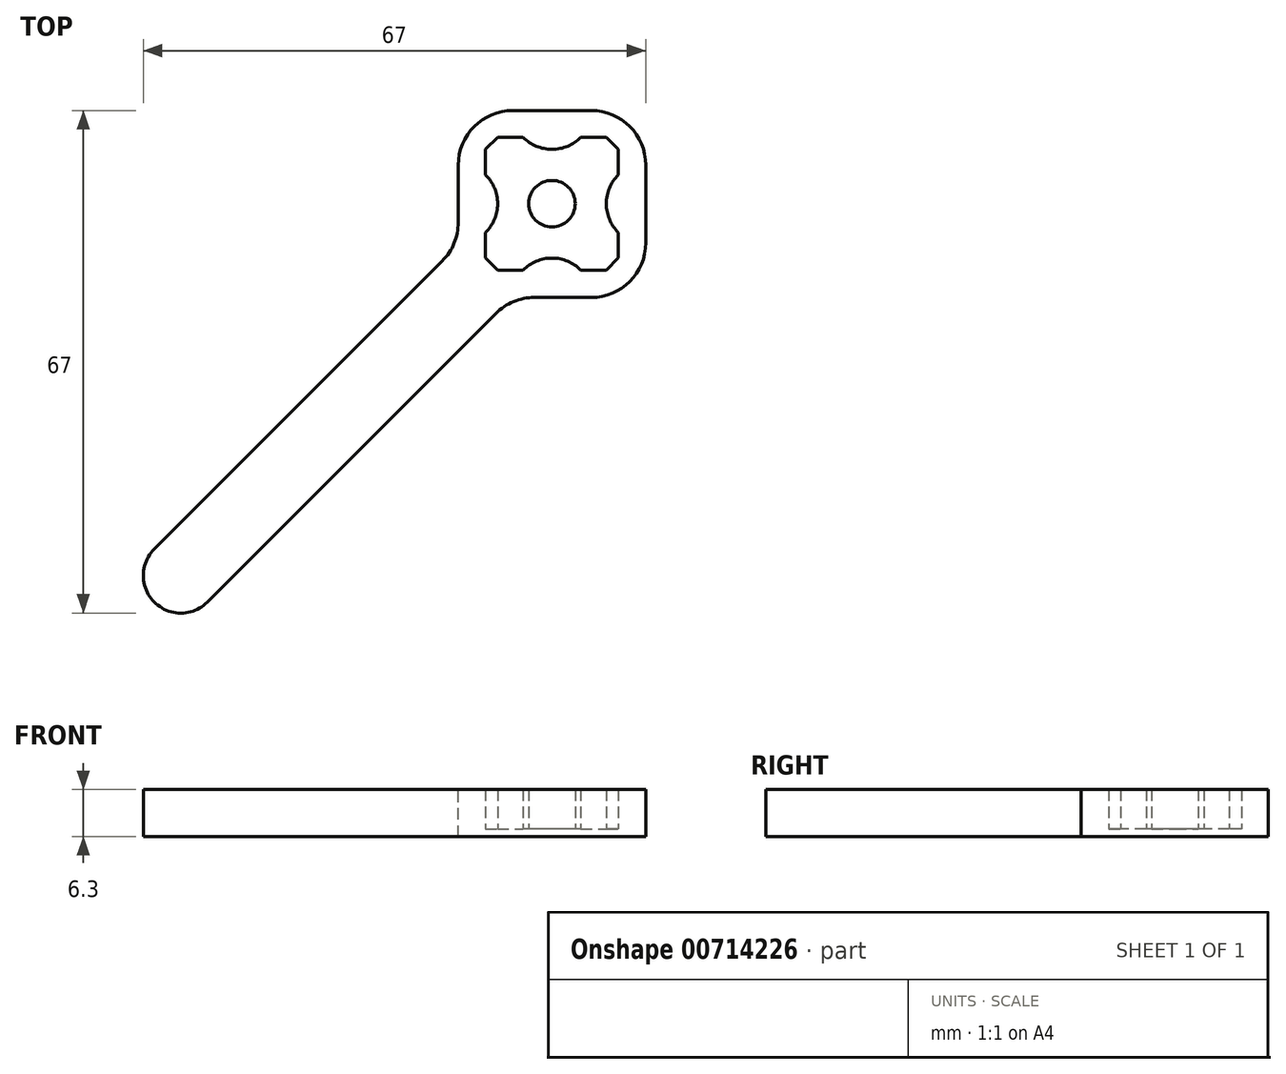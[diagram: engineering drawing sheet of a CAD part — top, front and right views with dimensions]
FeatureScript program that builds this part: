
annotation { "Feature Type Name" : "Feature", "Feature Type Description" : "" }
export const myFeature = defineFeature(function(context is Context, id is Id, definition is map)
    precondition{}
    {
        {
            var Q0;
            Q0=qCreatedBy(makeId("Top.planeOp"),FACE);
            var sketch = newSketch(context, id + "F0", { "sketchPlane" : qUnion([Q0])});
            skPoint(sketch, "E0", {"position": v(-49.5, -49.5) * mm});
            skArc(sketch, "E1", {"start": v(-53.03, -45.96) * mm, "mid": v(-53.03, -53.03) * mm, "end": v(-45.96, -53.03) * mm});
            skLineSegment(sketch, "E2", {"start": v(-5.35, -12.42) * mm, "end": v(-45.96, -53.03) * mm});
            skLineSegment(sketch, "E3", {"start": v(-53.03, -45.96) * mm, "end": v(-12.5, -5.43) * mm});
            skLineSegment(sketch, "E4.bottom", {"start": v(12.5, -12.5) * mm, "end": v(-5.43, -12.5) * mm});
            skLineSegment(sketch, "E4.top", {"start": v(12.5, 12.5) * mm, "end": v(-12.5, 12.5) * mm});
            skLineSegment(sketch, "E4.left", {"start": v(12.5, -12.5) * mm, "end": v(12.5, 12.5) * mm});
            skPoint(sketch, "E4.middle", {"position": v(0, 0) * mm});
            skLineSegment(sketch, "E5.bottom", {"start": v(12.5, 12.58) * mm, "end": v(-12.5, 12.58) * mm});
            skLineSegment(sketch, "E5.top", {"start": v(12.5, -12.42) * mm, "end": v(-5.35, -12.42) * mm});
            skLineSegment(sketch, "E5.left", {"start": v(12.5, 12.58) * mm, "end": v(12.5, -12.42) * mm});
            skLineSegment(sketch, "E5.right", {"start": v(-12.5, 12.58) * mm, "end": v(-12.5, -5.43) * mm});
            skPoint(sketch, "E5.middle", {"position": v(0, 0.08) * mm});
            skLineSegment(sketch, "E6.bottom", {"start": v(-7.25, 8.93) * mm, "end": v(-3.85, 8.93) * mm});
            skLineSegment(sketch, "E6.top", {"start": v(-7.25, -8.77) * mm, "end": v(-3.85, -8.77) * mm});
            skLineSegment(sketch, "E6.left", {"start": v(-8.85, 7.33) * mm, "end": v(-8.85, 3.93) * mm});
            skLineSegment(sketch, "E6.right", {"start": v(8.85, 7.33) * mm, "end": v(8.85, 3.93) * mm});
            skPoint(sketch, "E7", {"position": v(-3.85, 8.93) * mm});
            skPoint(sketch, "E8", {"position": v(3.85, 8.93) * mm});
            skPoint(sketch, "E9", {"position": v(8.85, 3.93) * mm});
            skPoint(sketch, "E10", {"position": v(8.85, -3.77) * mm});
            skPoint(sketch, "E11", {"position": v(3.85, -8.77) * mm});
            skPoint(sketch, "E12", {"position": v(-3.85, -8.77) * mm});
            skPoint(sketch, "E13", {"position": v(-8.85, -3.77) * mm});
            skPoint(sketch, "E14", {"position": v(-8.85, 3.93) * mm});
            skPoint(sketch, "E15", {"position": v(-7.25, 0.08) * mm});
            skPoint(sketch, "E16", {"position": v(0, 7.33) * mm});
            skPoint(sketch, "E17", {"position": v(7.25, 0.08) * mm});
            skPoint(sketch, "E18", {"position": v(0, -7.17) * mm});
            skArc(sketch, "E19", {"start": v(-3.85, 8.93) * mm, "mid": v(0, 7.33) * mm, "end": v(3.85, 8.93) * mm});
            skArc(sketch, "E20", {"start": v(8.85, 3.93) * mm, "mid": v(7.25, 0.08) * mm, "end": v(8.85, -3.77) * mm});
            skArc(sketch, "E21", {"start": v(3.85, -8.77) * mm, "mid": v(0, -7.17) * mm, "end": v(-3.85, -8.77) * mm});
            skArc(sketch, "E22", {"start": v(-8.85, -3.77) * mm, "mid": v(-7.25, 0.08) * mm, "end": v(-8.85, 3.93) * mm});
            skPoint(sketch, "E23.orphan", {"position": v(7.25, 7.33) * mm});
            skPoint(sketch, "E24.orphan", {"position": v(-7.25, 7.33) * mm});
            skPoint(sketch, "E25.orphan", {"position": v(-7.25, -7.17) * mm});
            skPoint(sketch, "E26.left.end.orphan", {"position": v(7.25, -7.17) * mm});
            skLineSegment(sketch, "E27.trimOffspring", {"start": v(3.85, 8.93) * mm, "end": v(7.25, 8.93) * mm});
            skLineSegment(sketch, "E28.trimOffspring", {"start": v(8.85, -3.77) * mm, "end": v(8.85, -7.17) * mm});
            skLineSegment(sketch, "E29.trimOffspring", {"start": v(3.85, -8.77) * mm, "end": v(7.25, -8.77) * mm});
            skLineSegment(sketch, "E30.trimOffspring", {"start": v(-8.85, -3.77) * mm, "end": v(-8.85, -7.17) * mm});
            skPoint(sketch, "E31", {"position": v(7.25, 8.93) * mm});
            skPoint(sketch, "E32", {"position": v(8.85, 7.33) * mm});
            skPoint(sketch, "E33", {"position": v(8.85, -7.17) * mm});
            skPoint(sketch, "E34", {"position": v(7.25, -8.77) * mm});
            skPoint(sketch, "E35", {"position": v(-7.25, -8.77) * mm});
            skPoint(sketch, "E36", {"position": v(-8.85, -7.17) * mm});
            skPoint(sketch, "E37", {"position": v(-8.85, 7.33) * mm});
            skPoint(sketch, "E38", {"position": v(-7.25, 8.93) * mm});
            skLineSegment(sketch, "E39", {"start": v(-8.85, 7.33) * mm, "end": v(-7.25, 8.93) * mm});
            skLineSegment(sketch, "E40", {"start": v(7.25, 8.93) * mm, "end": v(8.85, 7.33) * mm});
            skLineSegment(sketch, "E41", {"start": v(8.85, -7.17) * mm, "end": v(7.25, -8.77) * mm});
            skLineSegment(sketch, "E42", {"start": v(-8.85, -7.17) * mm, "end": v(-7.25, -8.77) * mm});
            skPoint(sketch, "E43.orphan", {"position": v(-8.85, -8.77) * mm});
            skPoint(sketch, "E44.orphan", {"position": v(8.85, -8.77) * mm});
            skPoint(sketch, "E45.orphan", {"position": v(8.85, 8.93) * mm});
            skPoint(sketch, "E46.orphan", {"position": v(-8.85, 8.93) * mm});
            skCircle(sketch, "E47", {"center": v(0, 0.08) * mm, "radius": 3.1 * mm});
            skLineSegment(sketch, "E48.trimOffspring", {"start": v(-12.5, -5.43) * mm, "end": v(-12.5, 12.5) * mm});
            skLineSegment(sketch, "E49.trimOffspring", {"start": v(-12.5, -12.42) * mm, "end": v(-12.5, -12.42) * mm});
            skPoint(sketch, "E4.right.start.orphan", {"position": v(-12.5, -12.5) * mm});
            skSolve(sketch);
        }
        {
            var Q0;
            {var subQ1=sQuery(id+"F0.wireOp",EDGE,"E1");Q0=makeQuery(id+"F0.imprint","IMPRINT",FACE,{"disambiguationData":[TD([[makeQuery(id+"F0.imprint","IMPRINT",EDGE,{"derivedFrom":subQ1}),1.0]])]});}
            var Q1;
            Q1=makeQuery(id+"F0.imprint","IMPRINT",FACE,{"disambiguationData":[TD([[makeQuery(id+"F0.imprint","IMPRINT",EDGE,{"derivedFrom":sQuery(id+"F0.wireOp",EDGE,"E6.bottom")}),-1.0]])]});
            var Q2;
            Q2=makeQuery(id+"F0.imprint","IMPRINT",FACE,{"disambiguationData":[TD([[makeQuery(id+"F0.imprint","IMPRINT",EDGE,{"derivedFrom":sQuery(id+"F0.wireOp",EDGE,"E47")}),1.0]])]});
            extrude(context, id + "F1", {"entities" : qUnion([Q0, Q1, Q2]), "oppositeDirection" : true, "depth" : 1 * mm, "offsetDistance" : 25 * mm});
        }
        {
            var Q0;
            {var subQ1=sQuery(id+"F0.wireOp",EDGE,"E1");Q0=makeQuery(id+"F0.imprint","IMPRINT",FACE,{"disambiguationData":[TD([[makeQuery(id+"F0.imprint","IMPRINT",EDGE,{"derivedFrom":subQ1}),1.0]])]});}
            var Q1;
            Q1=makeQuery(id+"F0.imprint","IMPRINT",FACE,{"disambiguationData":[TD([[makeQuery(id+"F0.imprint","IMPRINT",EDGE,{"derivedFrom":sQuery(id+"F0.wireOp",EDGE,"E47")}),1.0]])]});
            extrude(context, id + "F2", {"entities" : qUnion([Q0, Q1]), "operationType" : NewBodyOperationType.ADD, "depth" : 5.3 * mm, "offsetDistance" : 25 * mm});
        }
        {
            var Q0;
            {var subQ0=sQuery(id+"F0.wireOp",EDGE,"E48.trimOffspring");var subQ1=sQuery(id+"F0.wireOp",EDGE,"E3");Q0=makeQuery(id+"F2.boolean.opBoolean","MERGE",EDGE,{"derivedFrom":[makeQuery(id+"F1.opExtrude","SWEPT_EDGE",EDGE,{"disambiguationData":[OSD([subQ1,subQ0])]}),makeQuery(id+"F2.opExtrude","SWEPT_EDGE",EDGE,{"disambiguationData":[OSD([subQ1,subQ0])]})]});}
            var Q1;
            {var subQ0=sQuery(id+"F0.wireOp",EDGE,"E48.trimOffspring");var subQ1=sQuery(id+"F0.wireOp",EDGE,"E4.top");Q1=makeQuery(id+"F2.boolean.opBoolean","MERGE",EDGE,{"derivedFrom":[makeQuery(id+"F1.opExtrude","SWEPT_EDGE",EDGE,{"disambiguationData":[OSD([subQ1,subQ0])]}),makeQuery(id+"F2.opExtrude","SWEPT_EDGE",EDGE,{"disambiguationData":[OSD([subQ1,subQ0])]})]});}
            var Q2;
            {var subQ0=sQuery(id+"F0.wireOp",EDGE,"E5.left");var subQ1=sQuery(id+"F0.wireOp",EDGE,"E4.top");Q2=makeQuery(id+"F2.boolean.opBoolean","MERGE",EDGE,{"derivedFrom":[makeQuery(id+"F1.opExtrude","SWEPT_EDGE",EDGE,{"disambiguationData":[OSD([subQ1,subQ0])]}),makeQuery(id+"F2.opExtrude","SWEPT_EDGE",EDGE,{"disambiguationData":[OSD([subQ1,subQ0])]})]});}
            var Q3;
            {var subQ0=sQuery(id+"F0.wireOp",EDGE,"E5.left");var subQ1=sQuery(id+"F0.wireOp",EDGE,"E5.top");Q3=makeQuery(id+"F2.boolean.opBoolean","MERGE",EDGE,{"derivedFrom":[makeQuery(id+"F1.opExtrude","SWEPT_EDGE",EDGE,{"disambiguationData":[OSD([subQ1,subQ0])]}),makeQuery(id+"F2.opExtrude","SWEPT_EDGE",EDGE,{"disambiguationData":[OSD([subQ1,subQ0])]})]});}
            var Q4;
            {var subQ0=sQuery(id+"F0.wireOp",EDGE,"E5.top");var subQ1=sQuery(id+"F0.wireOp",EDGE,"E2");Q4=makeQuery(id+"F2.boolean.opBoolean","MERGE",EDGE,{"derivedFrom":[makeQuery(id+"F1.opExtrude","SWEPT_EDGE",EDGE,{"disambiguationData":[OSD([subQ1,subQ0])]}),makeQuery(id+"F2.opExtrude","SWEPT_EDGE",EDGE,{"disambiguationData":[OSD([subQ1,subQ0])]})]});}
            fillet(context, id + "F3", {"entities" : qUnion([Q0, Q1, Q2, Q3, Q4]), "radius" : 7.28 * mm, "tangentPropagation" : true, "allowEdgeOverflow" : false});
        }
    });
